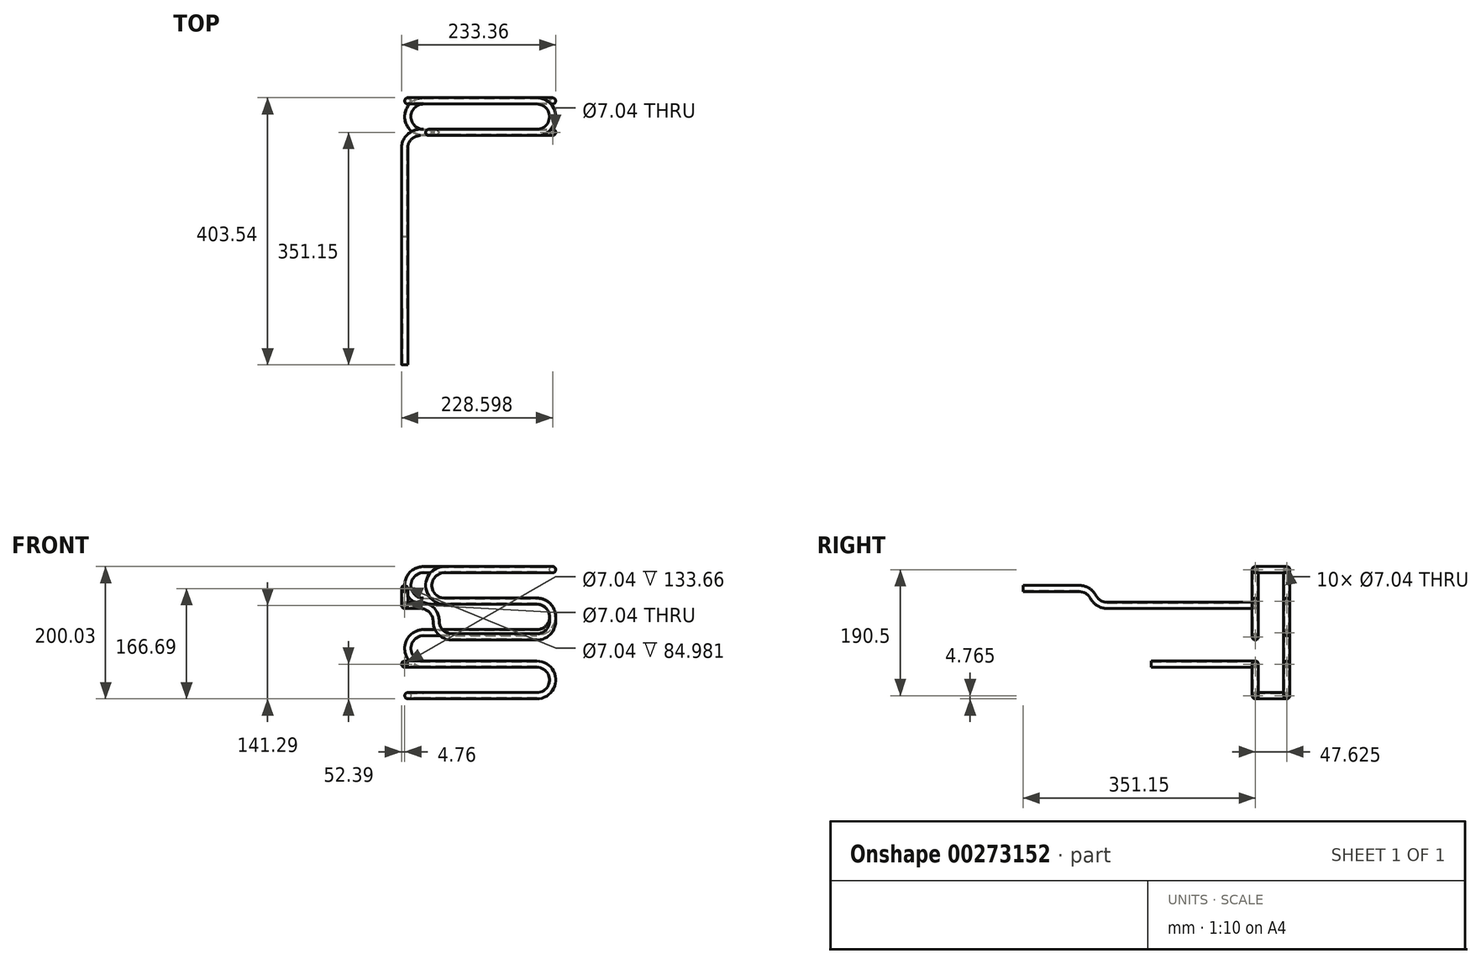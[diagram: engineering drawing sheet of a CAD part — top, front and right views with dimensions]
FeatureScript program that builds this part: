
annotation { "Feature Type Name" : "Feature", "Feature Type Description" : "" }
export const myFeature = defineFeature(function(context is Context, id is Id, definition is map)
    precondition{}
    {
        {
            var Q0;
            Q0=qCreatedBy(makeId("Front.planeOp"),FACE);
            var sketch = newSketch(context, id + "F0", { "sketchPlane" : qUnion([Q0])});
            skLineSegment(sketch, "E0", {"start": v(-55.73, 0) * mm, "end": v(115.72, 0) * mm});
            skArc(sketch, "E1", {"start": v(115.72, -47.63) * mm, "mid": v(139.53, -23.81) * mm, "end": v(115.72, 0) * mm});
            skLineSegment(sketch, "E2", {"start": v(115.72, -47.63) * mm, "end": v(-55.73, -47.63) * mm});
            skSolve(sketch);
        }
        {
            var Q0;
            Q0=qCreatedBy(makeId("Right.planeOp"),FACE);
            var Q1;
            Q1=sQuery(id+"F0.wireOp",VERTEX,"E0.start");
            cPlane(context, id + "F1", {"entities" : qUnion([Q0, Q1]), "cplaneType" : CPlaneType.PLANE_POINT, "offset" : 25.4 * mm, "width" : 152.4 * mm, "height" : 152.4 * mm});
        }
        {
            var Q0;
            Q0=qCreatedBy(id+"F1.planeOp",FACE);
            var sketch = newSketch(context, id + "F2", { "sketchPlane" : qUnion([Q0])});
            skCircle(sketch, "E3", {"center": v(0, 0) * mm, "radius": 4.76 * mm});
            skCircle(sketch, "E4", {"center": v(0, 0) * mm, "radius": 3.52 * mm});
            skSolve(sketch);
        }
        {
            var Q0;
            Q0=qSketchRegion(id+"F2",true);
            var Q1;
            Q1=qConstructionFilter(qBodyType(qCreatedBy(id+"F0",EDGE),BodyType.WIRE),ConstructionObject.NO);
            sweep(context, id + "F3", {"profiles" : qUnion([Q0]), "path" : qUnion([Q1])});
        }
        {
            var Q0;
            Q0=qCreatedBy(makeId("Top.planeOp"),FACE);
            cPlane(context, id + "F4", {"entities" : qUnion([Q0]), "cplaneType" : CPlaneType.OFFSET, "offset" : 47.62 * mm, "oppositeDirection" : true, "width" : 152.4 * mm, "height" : 152.4 * mm});
        }
        {
            var Q0;
            Q0=qCreatedBy(id+"F4.planeOp",FACE);
            var sketch = newSketch(context, id + "F5", { "sketchPlane" : qUnion([Q0])});
            skArc(sketch, "E5", {"start": v(-55.73, 47.63) * mm, "mid": v(-79.55, 23.81) * mm, "end": v(-55.73, 0) * mm});
            skSolve(sketch);
        }
        {
            var Q0;
            Q0=makeQuery(id+"F3.opSweep","CAP_FACE",FACE,{"disambiguationData":[OSD([sQuery(id+"F0.wireOp",VERTEX,"wHQo276Y-sBvi-N2un-N2Yk-hAijH3XrL1uE.end"),sQuery(id+"F2.wireOp",EDGE,"E3")])],"isStart":false});
            var sketch = newSketch(context, id + "F6", { "sketchPlane" : qUnion([Q0])});
            skCircle(sketch, "E6", {"center": v(0, -47.63) * mm, "radius": 4.76 * mm});
            skCircle(sketch, "E7", {"center": v(0, -47.63) * mm, "radius": 3.52 * mm});
            skSolve(sketch);
        }
        {
            var Q0;
            Q0=qSketchRegion(id+"F6",true);
            var Q1;
            Q1=qConstructionFilter(qBodyType(qCreatedBy(id+"F5",EDGE),BodyType.WIRE),ConstructionObject.NO);
            sweep(context, id + "F7", {"operationType" : NewBodyOperationType.ADD, "profiles" : qUnion([Q0]), "path" : qUnion([Q1])});
        }
        {
            var Q0;
            Q0=qCreatedBy(makeId("Front.planeOp"),FACE);
            cPlane(context, id + "F8", {"entities" : qUnion([Q0]), "cplaneType" : CPlaneType.OFFSET, "offset" : 47.62 * mm, "oppositeDirection" : true, "width" : 152.4 * mm, "height" : 152.4 * mm});
        }
        {
            var Q0;
            Q0=qCreatedBy(id+"F8.planeOp",FACE);
            var sketch = newSketch(context, id + "F9", { "sketchPlane" : qUnion([Q0])});
            skLineSegment(sketch, "E8", {"start": v(-55.73, -47.62) * mm, "end": v(115.72, -47.62) * mm});
            skArc(sketch, "E9", {"start": v(115.72, -47.63) * mm, "mid": v(139.53, -23.81) * mm, "end": v(115.72, 0) * mm});
            skLineSegment(sketch, "E10", {"start": v(115.72, 0) * mm, "end": v(-55.73, 0) * mm});
            skArc(sketch, "E11", {"start": v(-55.73, 47.62) * mm, "mid": v(-79.55, 23.81) * mm, "end": v(-55.73, 0) * mm});
            skLineSegment(sketch, "E12", {"start": v(-55.73, 47.62) * mm, "end": v(115.72, 47.62) * mm});
            skArc(sketch, "E13", {"start": v(115.72, 47.62) * mm, "mid": v(139.53, 71.44) * mm, "end": v(115.72, 95.25) * mm});
            skLineSegment(sketch, "E14", {"start": v(115.72, 95.25) * mm, "end": v(-55.73, 95.25) * mm});
            skArc(sketch, "E15", {"start": v(-55.73, 142.88) * mm, "mid": v(-79.55, 119.06) * mm, "end": v(-55.73, 95.25) * mm});
            skLineSegment(sketch, "E16", {"start": v(-55.73, 142.88) * mm, "end": v(115.72, 142.88) * mm});
            skSolve(sketch);
        }
        {
            var Q0;
            Q0=makeQuery(id+"F7.opSweep","CAP_FACE",FACE,{"disambiguationData":[OSD([sQuery(id+"F5.wireOp",VERTEX,"ypTdSRva-W3zM-n7zO-EWnq-FCaz20HJjr4Y.end"),sQuery(id+"F6.wireOp",EDGE,"E6")])],"isStart":false});
            var sketch = newSketch(context, id + "F10", { "sketchPlane" : qUnion([Q0])});
            skCircle(sketch, "E17", {"center": v(47.63, -47.63) * mm, "radius": 4.76 * mm});
            skCircle(sketch, "E18", {"center": v(47.63, -47.63) * mm, "radius": 3.52 * mm});
            skSolve(sketch);
        }
        {
            var Q0;
            Q0=qSketchRegion(id+"F10",true);
            var Q1;
            Q1=qConstructionFilter(qBodyType(qCreatedBy(id+"F9",EDGE),BodyType.WIRE),ConstructionObject.NO);
            sweep(context, id + "F11", {"operationType" : NewBodyOperationType.ADD, "profiles" : qUnion([Q0]), "path" : qUnion([Q1])});
        }
        {
            var Q0;
            Q0=qCreatedBy(id+"F4.planeOp",FACE);
            cPlane(context, id + "F12", {"entities" : qUnion([Q0]), "cplaneType" : CPlaneType.OFFSET, "offset" : 190.5 * mm, "width" : 152.4 * mm, "height" : 152.4 * mm});
        }
        {
            var Q0;
            Q0=makeQuery(id+"F11.opSweep","CAP_FACE",FACE,{"disambiguationData":[OSD([sQuery(id+"F9.wireOp",VERTEX,"E16.end"),sQuery(id+"F10.wireOp",EDGE,"E17"),sQuery(id+"F10.wireOp",EDGE,"E18")])],"isStart":false});
            var sketch = newSketch(context, id + "F13", { "sketchPlane" : qUnion([Q0])});
            skCircle(sketch, "E19", {"center": v(47.63, 142.88) * mm, "radius": 3.52 * mm});
            skCircle(sketch, "E20", {"center": v(47.63, 142.88) * mm, "radius": 4.76 * mm});
            skSolve(sketch);
        }
        {
            var Q0;
            Q0=qCreatedBy(id+"F12.planeOp",FACE);
            var sketch = newSketch(context, id + "F14", { "sketchPlane" : qUnion([Q0])});
            skArc(sketch, "E21", {"start": v(115.72, 0) * mm, "mid": v(139.53, 23.81) * mm, "end": v(115.72, 47.63) * mm});
            skSolve(sketch);
        }
        {
            var Q0;
            Q0 = qSketchRegion(id + "F13", true);
            var Q1;
            Q1 = qConstructionFilter(qBodyType(qCreatedBy(id + "F14" ,EDGE), BodyType.WIRE), ConstructionObject.NO);
            sweep(context, id + "F15", {"operationType" : NewBodyOperationType.ADD, "profiles" : qUnion([Q0]), "path" : qUnion([Q1])});
        }
        {
            var Q0;
            Q0=makeQuery(id+"F3.opSweep","CAP_FACE",FACE,{"disambiguationData":[OSD([sQuery(id+"F0.wireOp",VERTEX,"E0.start"),sQuery(id+"F2.wireOp",EDGE,"E3"),sQuery(id+"F2.wireOp",EDGE,"E4")])],"isStart":true});
            var sketch = newSketch(context, id + "F16", { "sketchPlane" : qUnion([Q0])});
            skCircle(sketch, "E22", {"center": v(0, 0) * mm, "radius": 3.52 * mm});
            skCircle(sketch, "E23", {"center": v(0, 0) * mm, "radius": 4.76 * mm});
            skSolve(sketch);
        }
        {
            var Q0;
            Q0 = qSketchRegion(id + "F16", true);
            extrude(context, id + "F17", {"entities" : qUnion([Q0]), "operationType" : NewBodyOperationType.ADD, "depth" : 73.02 * mm});
        }
        {
            var Q0;
            Q0=makeQuery(id+"F15.opSweep","CAP_FACE",FACE,{"disambiguationData":[OSD([sQuery(id+"F13.wireOp",EDGE,"E19"),sQuery(id+"F13.wireOp",EDGE,"E20"),sQuery(id+"F14.wireOp",VERTEX,"E21.start")])],"isStart":false});
            var sketch = newSketch(context, id + "F18", { "sketchPlane" : qUnion([Q0])});
            skCircle(sketch, "E24", {"center": v(0, 142.88) * mm, "radius": 3.52 * mm});
            skCircle(sketch, "E25", {"center": v(0, 142.88) * mm, "radius": 4.76 * mm});
            skSolve(sketch);
        }
        {
            var Q0;
            Q0=qCreatedBy(makeId("Front.planeOp"),FACE);
            var sketch = newSketch(context, id + "F19", { "sketchPlane" : qUnion([Q0])});
            skLineSegment(sketch, "E26", {"start": v(115.72, 142.88) * mm, "end": v(-23.98, 142.88) * mm});
            skArc(sketch, "E27", {"start": v(-23.98, 142.88) * mm, "mid": v(-47.8, 119.06) * mm, "end": v(-23.98, 95.25) * mm});
            skLineSegment(sketch, "E28", {"start": v(-23.98, 95.25) * mm, "end": v(115.72, 95.25) * mm});
            skLineSegment(sketch, "E29", {"start": v(115.72, 41.28) * mm, "end": v(-12.87, 41.28) * mm});
            skArc(sketch, "E30", {"start": v(-36.68, 65.09) * mm, "mid": v(-29.71, 48.25) * mm, "end": v(-12.87, 41.28) * mm});
            skArc(sketch, "E31", {"start": v(-36.68, 65.09) * mm, "mid": v(-43.66, 81.93) * mm, "end": v(-60.5, 88.9) * mm});
            skArc(sketch, "E32", {"start": v(139.53, 71.44) * mm, "mid": v(132.55, 88.28) * mm, "end": v(115.72, 95.25) * mm});
            skLineSegment(sketch, "E33", {"start": v(139.53, 71.44) * mm, "end": v(139.53, 65.09) * mm});
            skArc(sketch, "E34", {"start": v(115.72, 41.28) * mm, "mid": v(132.55, 48.25) * mm, "end": v(139.53, 65.09) * mm});
            skSolve(sketch);
        }
        {
            var Q0;
            Q0 = qSketchRegion(id + "F18", true);
            var Q1;
            Q1 = qConstructionFilter(qBodyType(qCreatedBy(id + "F19" ,EDGE), BodyType.WIRE), ConstructionObject.NO);
            sweep(context, id + "F20", {"operationType" : NewBodyOperationType.ADD, "profiles" : qUnion([Q0]), "path" : qUnion([Q1])});
        }
        {
            var Q0;
            Q0=qCreatedBy(id+"F4.planeOp",FACE);
            cPlane(context, id + "F21", {"entities" : qUnion([Q0]), "cplaneType" : CPlaneType.OFFSET, "offset" : 136.53 * mm, "width" : 152.4 * mm, "height" : 152.4 * mm});
        }
        {
            var Q0;
            Q0=qCreatedBy(id+"F21.planeOp",FACE);
            var sketch = newSketch(context, id + "F22", { "sketchPlane" : qUnion([Q0])});
            skArc(sketch, "E35", {"start": v(-60.5, 0) * mm, "mid": v(-77.34, -6.97) * mm, "end": v(-84.3, -23.81) * mm});
            skSolve(sketch);
        }
        {
            var Q0;
            Q0=makeQuery(id+"F20.opSweep","CAP_FACE",FACE,{"disambiguationData":[OSD([sQuery(id+"F18.wireOp",EDGE,"E24"),sQuery(id+"F18.wireOp",EDGE,"E25"),sQuery(id+"F19.wireOp",VERTEX,"E31.end")])],"isStart":false});
            var sketch = newSketch(context, id + "F23", { "sketchPlane" : qUnion([Q0])});
            skCircle(sketch, "E36", {"center": v(0, 88.9) * mm, "radius": 3.52 * mm});
            skCircle(sketch, "E37", {"center": v(0, 88.9) * mm, "radius": 4.76 * mm});
            skSolve(sketch);
        }
        {
            var Q0;
            Q0 = qSketchRegion(id + "F23", true);
            var Q1;
            Q1 = qConstructionFilter(qBodyType(qCreatedBy(id + "F22" ,EDGE), BodyType.WIRE), ConstructionObject.NO);
            sweep(context, id + "F24", {"operationType" : NewBodyOperationType.ADD, "profiles" : qUnion([Q0]), "path" : qUnion([Q1])});
        }
        {
            var Q0;
            Q0=makeQuery(id+"F17.opExtrude","CAP_FACE",FACE,{"disambiguationData":[OSD([sQuery(id+"F16.wireOp",EDGE,"E22"),sQuery(id+"F16.wireOp",EDGE,"E23")])],"isStart":false});
            var sketch = newSketch(context, id + "F25", { "sketchPlane" : qUnion([Q0])});
            skCircle(sketch, "E38", {"center": v(0, 0) * mm, "radius": 6.2 * mm});
            skSolve(sketch);
        }
        {
            var Q0;
            Q0 = qSketchRegion(id + "F25", true);
            extrude(context, id + "F26", {"entities" : qUnion([Q0]), "operationType" : NewBodyOperationType.REMOVE, "oppositeDirection" : true, "depth" : 68.26 * mm});
        }
        {
            var Q0;
            Q0=qCreatedBy(id+"F4.planeOp",FACE);
            cPlane(context, id + "F27", {"entities" : qUnion([Q0]), "cplaneType" : CPlaneType.OFFSET, "offset" : 47.62 * mm, "width" : 152.4 * mm, "height" : 152.4 * mm});
        }
        {
            var Q0;
            Q0=qCreatedBy(id+"F27.planeOp",FACE);
            var sketch = newSketch(context, id + "F28", { "sketchPlane" : qUnion([Q0])});
            skArc(sketch, "E39", {"start": v(-60.5, 0) * mm, "mid": v(-77.34, -6.97) * mm, "end": v(-84.3, -23.81) * mm});
            skSolve(sketch);
        }
        {
            var Q0;
            Q0=makeQuery(id+"F26.boolean.opBoolean","COPY",FACE,{"derivedFrom":makeQuery(id+"F26.opExtrude","CAP_FACE",FACE,{"disambiguationData":[OSD([sQuery(id+"F25.wireOp",EDGE,"E38")])],"isStart":false})});
            var sketch = newSketch(context, id + "F29", { "sketchPlane" : qUnion([Q0])});
            skCircle(sketch, "E40", {"center": v(0, 0) * mm, "radius": 3.52 * mm});
            skCircle(sketch, "E41", {"center": v(0, 0) * mm, "radius": 4.76 * mm});
            skSolve(sketch);
        }
        {
            var Q0;
            Q0 = qSketchRegion(id + "F29", true);
            var Q1;
            Q1 = qConstructionFilter(qBodyType(qCreatedBy(id + "F28" ,EDGE), BodyType.WIRE), ConstructionObject.NO);
            sweep(context, id + "F30", {"operationType" : NewBodyOperationType.ADD, "profiles" : qUnion([Q0]), "path" : qUnion([Q1])});
        }
        {
            var Q0;
            Q0=makeQuery(id+"F30.opSweep","CAP_FACE",FACE,{"disambiguationData":[OSD([sQuery(id+"F28.wireOp",VERTEX,"E39.end"),sQuery(id+"F29.wireOp",EDGE,"E40"),sQuery(id+"F29.wireOp",EDGE,"E41")])],"isStart":false});
            var sketch = newSketch(context, id + "F31", { "sketchPlane" : qUnion([Q0])});
            skCircle(sketch, "E42", {"center": v(-84.3, 0) * mm, "radius": 3.52 * mm});
            skCircle(sketch, "E43", {"center": v(-84.3, 0) * mm, "radius": 4.76 * mm});
            skSolve(sketch);
        }
        {
            var Q0;
            Q0 = qSketchRegion(id + "F31", true);
            extrude(context, id + "F32", {"entities" : qUnion([Q0]), "operationType" : NewBodyOperationType.ADD, "depth" : 133.66 * mm});
        }
        {
            var Q0;
            Q0=makeQuery(id+"F24.opSweep","CAP_FACE",FACE,{"disambiguationData":[OSD([sQuery(id+"F22.wireOp",VERTEX,"E35.end"),sQuery(id+"F23.wireOp",EDGE,"E36"),sQuery(id+"F23.wireOp",EDGE,"E37")])],"isStart":false});
            var sketch = newSketch(context, id + "F33", { "sketchPlane" : qUnion([Q0])});
            skCircle(sketch, "E44", {"center": v(-84.3, 88.9) * mm, "radius": 4.76 * mm});
            skCircle(sketch, "E45", {"center": v(-84.3, 88.9) * mm, "radius": 3.52 * mm});
            skSolve(sketch);
        }
        {
            var Q0;
            Q0 = qSketchRegion(id + "F33", true);
            extrude(context, id + "F34", {"entities" : qUnion([Q0]), "operationType" : NewBodyOperationType.ADD, "depth" : 200.23 * mm});
        }
        {
            var Q0;
            Q0=qCreatedBy(id+"F1.planeOp",FACE);
            cPlane(context, id + "F35", {"entities" : qUnion([Q0]), "cplaneType" : CPlaneType.OFFSET, "offset" : 28.57 * mm, "oppositeDirection" : true, "width" : 152.4 * mm, "height" : 152.4 * mm});
        }
        {
            var Q0;
            Q0=qCreatedBy(id+"F35.planeOp",FACE);
            var sketch = newSketch(context, id + "F36", { "sketchPlane" : qUnion([Q0])});
            skArc(sketch, "E46", {"start": v(-245.1, 101.6) * mm, "mid": v(-236.34, 92.32) * mm, "end": v(-224.05, 88.9) * mm});
            skArc(sketch, "E47", {"start": v(-245.1, 101.6) * mm, "mid": v(-253.87, 110.88) * mm, "end": v(-266.17, 114.3) * mm});
            skLineSegment(sketch, "E48", {"start": v(-266.17, 114.3) * mm, "end": v(-351.15, 114.3) * mm});
            skSolve(sketch);
        }
        {
            var Q0;
            Q0=makeQuery(id+"F34.opExtrude","CAP_FACE",FACE,{"disambiguationData":[OSD([sQuery(id+"F33.wireOp",EDGE,"E44"),sQuery(id+"F33.wireOp",EDGE,"E45")])],"isStart":false});
            var sketch = newSketch(context, id + "F37", { "sketchPlane" : qUnion([Q0])});
            skCircle(sketch, "E49", {"center": v(-84.3, 88.9) * mm, "radius": 3.52 * mm});
            skCircle(sketch, "E50", {"center": v(-84.3, 88.9) * mm, "radius": 4.76 * mm});
            skSolve(sketch);
        }
        {
            var Q0;
            Q0 = qSketchRegion(id + "F37", true);
            var Q1;
            Q1 = qConstructionFilter(qBodyType(qCreatedBy(id + "F36" ,EDGE), BodyType.WIRE), ConstructionObject.NO);
            sweep(context, id + "F38", {"operationType" : NewBodyOperationType.ADD, "profiles" : qUnion([Q0]), "path" : qUnion([Q1])});
        }
    });
